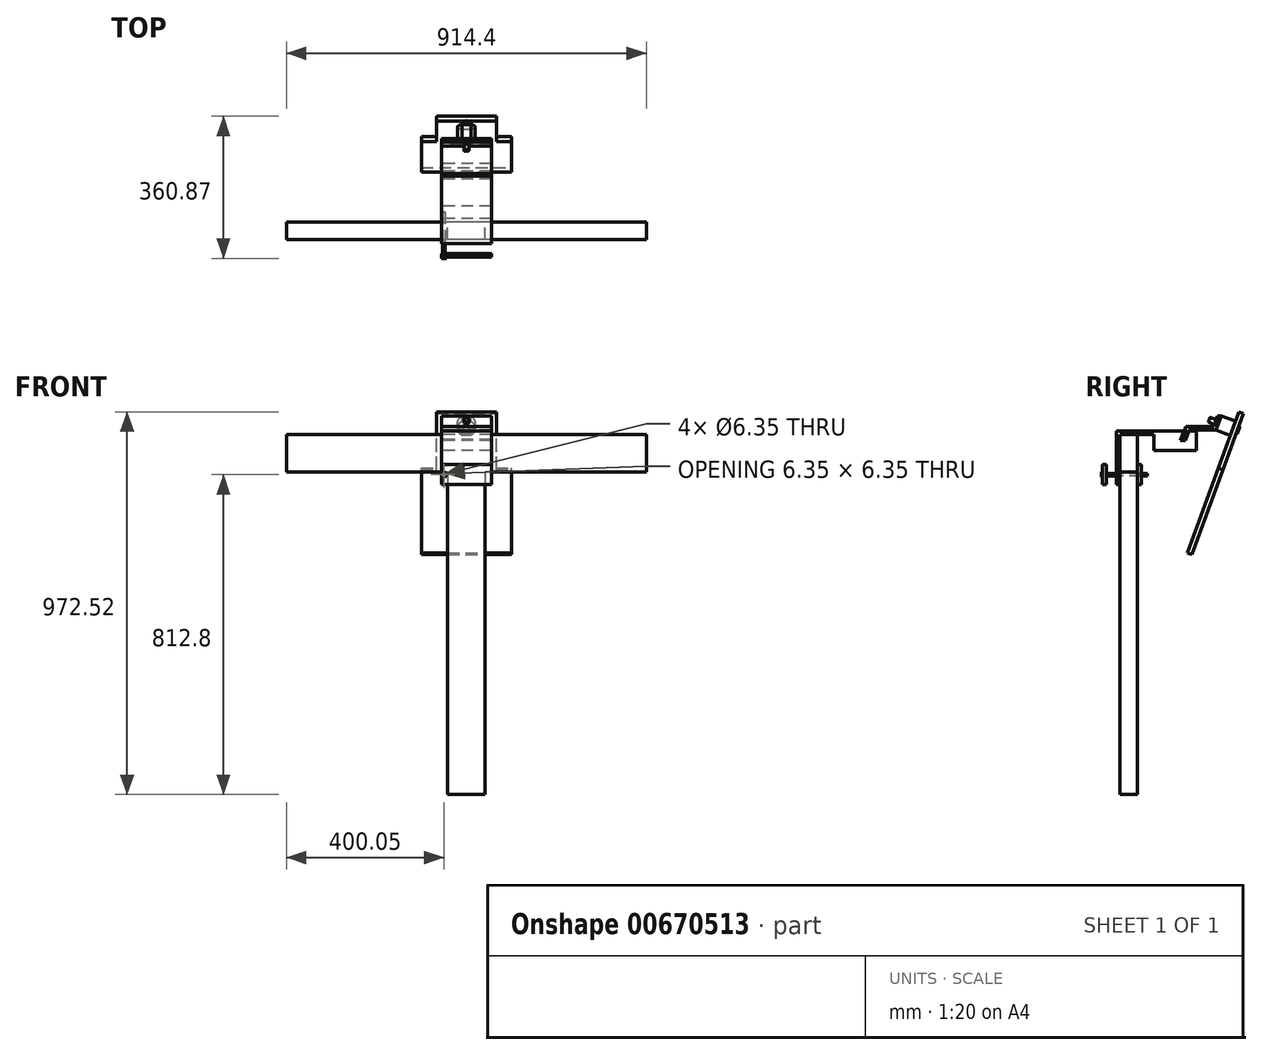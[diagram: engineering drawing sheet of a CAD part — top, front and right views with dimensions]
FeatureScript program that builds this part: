
annotation { "Feature Type Name" : "Feature", "Feature Type Description" : "" }
export const myFeature = defineFeature(function(context is Context, id is Id, definition is map)
    precondition{}
    {
        {
            var Q0;
            Q0=qCreatedBy(makeId("Right.planeOp"),FACE);
            var sketch = newSketch(context, id + "F0", { "sketchPlane" : qUnion([Q0])});
            skLineSegment(sketch, "E0.bottom", {"start": v(-44.45, 0) * mm, "end": v(0, 0) * mm});
            skLineSegment(sketch, "E0.top", {"start": v(-44.45, -914.4) * mm, "end": v(0, -914.4) * mm});
            skLineSegment(sketch, "E0.left", {"start": v(-44.45, 0) * mm, "end": v(-44.45, -914.4) * mm});
            skLineSegment(sketch, "E0.right", {"start": v(0, 0) * mm, "end": v(0, -914.4) * mm});
            skLineSegment(sketch, "E1.bottom", {"start": v(-53.97, 0) * mm, "end": v(149.23, 0) * mm});
            skLineSegment(sketch, "E1.top", {"start": v(-53.97, 9.52) * mm, "end": v(149.23, 9.53) * mm});
            skLineSegment(sketch, "E1.left", {"start": v(-53.98, 0) * mm, "end": v(-53.98, 9.53) * mm});
            skLineSegment(sketch, "E1.right", {"start": v(149.23, 0) * mm, "end": v(149.23, 9.53) * mm});
            skLineSegment(sketch, "E2.bottom", {"start": v(-53.97, 0) * mm, "end": v(-44.45, 0) * mm});
            skLineSegment(sketch, "E2.top", {"start": v(-53.97, -127) * mm, "end": v(-44.45, -127) * mm});
            skLineSegment(sketch, "E2.left", {"start": v(-53.97, 0) * mm, "end": v(-53.97, -127) * mm});
            skLineSegment(sketch, "E2.right", {"start": v(-44.45, 0) * mm, "end": v(-44.45, -127) * mm});
            skLineSegment(sketch, "E3.bottom", {"start": v(149.23, 0) * mm, "end": v(41.28, 0) * mm});
            skLineSegment(sketch, "E3.top", {"start": v(149.23, -39.75) * mm, "end": v(41.28, -39.75) * mm});
            skLineSegment(sketch, "E3.left", {"start": v(149.23, 0) * mm, "end": v(149.23, -39.75) * mm});
            skLineSegment(sketch, "E3.right", {"start": v(41.28, 0) * mm, "end": v(41.28, -39.75) * mm});
            skLineSegment(sketch, "E4", {"start": v(126.16, 33.39) * mm, "end": v(108.78, -14.35) * mm});
            skLineSegment(sketch, "E5", {"start": v(108.78, -14.35) * mm, "end": v(121.48, -14.35) * mm});
            skLineSegment(sketch, "E6", {"start": v(121.48, -14.35) * mm, "end": v(138.86, 33.39) * mm});
            skLineSegment(sketch, "E7.bottom", {"start": v(0, -127) * mm, "end": v(9.53, -127) * mm});
            skLineSegment(sketch, "E7.top", {"start": v(0, -76.2) * mm, "end": v(9.53, -76.2) * mm});
            skLineSegment(sketch, "E7.left", {"start": v(0, -127) * mm, "end": v(0, -76.2) * mm});
            skLineSegment(sketch, "E7.right", {"start": v(9.53, -127) * mm, "end": v(9.53, -76.2) * mm});
            skLineSegment(sketch, "E8", {"start": v(126.16, 33.39) * mm, "end": v(138.86, 33.39) * mm});
            skPoint(sketch, "E9", {"position": v(130.18, 9.52) * mm});
            skLineSegment(sketch, "E10", {"start": v(111.19, -11.81) * mm, "end": v(120.71, -11.81) * mm});
            skLineSegment(sketch, "E11", {"start": v(120.71, -11.81) * mm, "end": v(132.66, 21) * mm});
            skLineSegment(sketch, "E12", {"start": v(132.66, 21) * mm, "end": v(123.13, 21) * mm});
            skLineSegment(sketch, "E13", {"start": v(123.13, 21) * mm, "end": v(111.19, -11.81) * mm});
            skLineSegment(sketch, "E14.bottom", {"start": v(123.13, 21) * mm, "end": v(199.33, 21) * mm});
            skLineSegment(sketch, "E14.top", {"start": v(123.13, 11.48) * mm, "end": v(199.33, 11.48) * mm});
            skLineSegment(sketch, "E14.left", {"start": v(123.13, 21) * mm, "end": v(123.13, 11.48) * mm});
            skLineSegment(sketch, "E14.right", {"start": v(199.33, 21) * mm, "end": v(199.33, 11.48) * mm});
            skLineSegment(sketch, "E15", {"start": v(199.33, 11.48) * mm, "end": v(189.8, 11.48) * mm});
            skLineSegment(sketch, "E16", {"start": v(189.8, 11.48) * mm, "end": v(202.84, 47.29) * mm});
            skLineSegment(sketch, "E17", {"start": v(202.84, 47.29) * mm, "end": v(212.36, 47.29) * mm});
            skLineSegment(sketch, "E18", {"start": v(212.36, 47.29) * mm, "end": v(199.33, 11.48) * mm});
            skLineSegment(sketch, "E19.bottom", {"start": v(-88.9, -127) * mm, "end": v(-79.37, -127) * mm});
            skLineSegment(sketch, "E19.top", {"start": v(-88.9, -76.2) * mm, "end": v(-79.37, -76.2) * mm});
            skLineSegment(sketch, "E19.left", {"start": v(-88.9, -127) * mm, "end": v(-88.9, -76.2) * mm});
            skLineSegment(sketch, "E19.right", {"start": v(-79.37, -127) * mm, "end": v(-79.37, -76.2) * mm});
            skLineSegment(sketch, "E20.top", {"start": v(-44.45, -95.25) * mm, "end": v(0, -95.25) * mm});
            skLineSegment(sketch, "E20.left", {"start": v(-44.45, 0) * mm, "end": v(-44.45, -95.25) * mm});
            skLineSegment(sketch, "E20.right", {"start": v(0, 0) * mm, "end": v(0, -95.25) * mm});
            skSolve(sketch);
        }
        {
            var Q0;
            {var subQ1=sQuery(id+"F0.wireOp",EDGE,"E0.top");Q0=makeQuery(id+"F0.imprint","IMPRINT",FACE,{"disambiguationData":[TD([[makeQuery(id+"F0.imprint","IMPRINT",EDGE,{"derivedFrom":subQ1}),1.0]])]});}
            extrude(context, id + "F1", {"entities" : qUnion([Q0]), "depth" : 95.25 * mm, "offsetDistance" : 25.4 * mm, "symmetric" : true});
        }
        {
            var Q0;
            {var subQ2=sQuery(id+"F0.wireOp",EDGE,"E0.bottom");Q0=makeQuery(id+"F0.imprint","IMPRINT",FACE,{"disambiguationData":[TD([[makeQuery(id+"F0.imprint","IMPRINT",EDGE,{"derivedFrom":subQ2}),-1.0]])]});}
            extrude(context, id + "F2", {"entities" : qUnion([Q0]), "operationType" : NewBodyOperationType.ADD, "depth" : 914.4 * mm, "offsetDistance" : 25.4 * mm, "symmetric" : true});
        }
        {
            var Q0;
            {var subQ0=sQuery(id+"F0.wireOp",EDGE,"E2.top");Q0=makeQuery(id+"F0.imprint","IMPRINT",FACE,{"disambiguationData":[TD([[makeQuery(id+"F0.imprint","IMPRINT",EDGE,{"derivedFrom":subQ0}),1.0]])]});}
            var Q1;
            {var subQ1=sQuery(id+"F0.wireOp",EDGE,"E0.bottom");Q1=makeQuery(id+"F0.imprint","IMPRINT",FACE,{"disambiguationData":[TD([[makeQuery(id+"F0.imprint","IMPRINT",EDGE,{"derivedFrom":subQ1}),1.0]])]});}
            var Q2;
            Q2=makeQuery(id+"F0.imprint","IMPRINT",FACE,{"disambiguationData":[TD([[makeQuery(id+"F0.imprint","IMPRINT",EDGE,{"derivedFrom":sQuery(id+"F0.wireOp",EDGE,"E3.top")}),-1.0]])]});
            var Q3;
            {var subQ0=sQuery(id+"F0.wireOp",EDGE,"E1.right");Q3=makeQuery(id+"F0.imprint","IMPRINT",FACE,{"disambiguationData":[TD([[makeQuery(id+"F0.imprint","IMPRINT",EDGE,{"derivedFrom":subQ0}),1.0]])]});}
            var Q4;
            {var subQ3=sQuery(id+"F0.wireOp",EDGE,"E7.bottom");Q4=makeQuery(id+"F0.imprint","IMPRINT",FACE,{"disambiguationData":[TD([[makeQuery(id+"F0.imprint","IMPRINT",EDGE,{"derivedFrom":subQ3}),1.0]])]});}
            var Q5;
            Q5=makeQuery(id+"F0.imprint","IMPRINT",FACE,{"disambiguationData":[TD([[makeQuery(id+"F0.imprint","IMPRINT",EDGE,{"derivedFrom":sQuery(id+"F0.wireOp",EDGE,"E19.bottom")}),1.0]])]});
            extrude(context, id + "F3", {"entities" : qUnion([Q0, Q1, Q2, Q3, Q4, Q5]), "depth" : 127 * mm, "offsetDistance" : 25.4 * mm, "symmetric" : true});
        }
        {
            var Q0;
            {var subQ4=sQuery(id+"F0.wireOp",EDGE,"E14.right");Q0=makeQuery(id+"F0.imprint","IMPRINT",FACE,{"disambiguationData":[TD([[makeQuery(id+"F0.imprint","IMPRINT",EDGE,{"derivedFrom":subQ4}),1.0]])]});}
            var Q1;
            {var subQ0=sQuery(id+"F0.wireOp",EDGE,"E14.right");Q1=makeQuery(id+"F0.imprint","IMPRINT",FACE,{"disambiguationData":[TD([[makeQuery(id+"F0.imprint","IMPRINT",EDGE,{"derivedFrom":subQ0}),-1.0]])]});}
            var Q2;
            {var subQ0=sQuery(id+"F0.wireOp",EDGE,"E14.top");var subQ1=sQuery(id+"F0.wireOp",EDGE,"E6");var subQ2=makeQuery(id+"F0.imprint","INTERSECT",VERTEX,{"derivedFrom":[subQ1,subQ0]});Q2=makeQuery(id+"F0.imprint","IMPRINT",FACE,{"disambiguationData":[TD([[makeQuery(id+"F0.imprint","IMPRINT",EDGE,{"disambiguationData":[TD([[subQ2,-1.0]])],"derivedFrom":subQ1}),1.0]])]});}
            var Q3;
            {var subQ3=sQuery(id+"F0.wireOp",EDGE,"E12");Q3=makeQuery(id+"F0.imprint","IMPRINT",FACE,{"disambiguationData":[TD([[makeQuery(id+"F0.imprint","IMPRINT",EDGE,{"derivedFrom":subQ3}),1.0]])]});}
            var Q4;
            {var subQ3=sQuery(id+"F0.wireOp",EDGE,"E14.left");Q4=makeQuery(id+"F0.imprint","IMPRINT",FACE,{"disambiguationData":[TD([[makeQuery(id+"F0.imprint","IMPRINT",EDGE,{"derivedFrom":subQ3}),-1.0]])]});}
            var Q5;
            {var subQ0=sQuery(id+"F0.wireOp",EDGE,"E13");var subQ1=sQuery(id+"F0.wireOp",EDGE,"E1.bottom");var subQ2=makeQuery(id+"F0.imprint","INTERSECT",VERTEX,{"derivedFrom":[subQ1,subQ0]});Q5=makeQuery(id+"F0.imprint","IMPRINT",FACE,{"disambiguationData":[TD([[makeQuery(id+"F0.imprint","IMPRINT",EDGE,{"disambiguationData":[TD([[subQ2,-1.0]])],"derivedFrom":subQ1}),1.0]])]});}
            var Q6;
            {var subQ5=sQuery(id+"F0.wireOp",EDGE,"E10");Q6=makeQuery(id+"F0.imprint","IMPRINT",FACE,{"disambiguationData":[TD([[makeQuery(id+"F0.imprint","IMPRINT",EDGE,{"derivedFrom":subQ5}),1.0]])]});}
            var Q7;
            {var subQ0=sQuery(id+"F0.wireOp",EDGE,"E14.top");var subQ1=sQuery(id+"F0.wireOp",EDGE,"E6");var subQ2=makeQuery(id+"F0.imprint","INTERSECT",VERTEX,{"derivedFrom":[subQ1,subQ0]});Q7=makeQuery(id+"F0.imprint","IMPRINT",FACE,{"disambiguationData":[TD([[makeQuery(id+"F0.imprint","IMPRINT",EDGE,{"disambiguationData":[TD([[subQ2,-1.0]])],"derivedFrom":subQ1}),-1.0]])]});}
            extrude(context, id + "F4", {"entities" : qUnion([Q0, Q1, Q2, Q3, Q4, Q5, Q6, Q7]), "depth" : 127 * mm, "offsetDistance" : 25.4 * mm, "symmetric" : true});
        }
        {
            var Q0;
            Q0=makeQuery(id+"F4.opExtrude","SWEPT_FACE",FACE,{"disambiguationData":[OSD([sQuery(id+"F0.wireOp",EDGE,"E18")])]});
            var sketch = newSketch(context, id + "F5", { "sketchPlane" : qUnion([Q0])});
            skCircle(sketch, "E21", {"center": v(0, 98.02) * mm, "radius": 6.35 * mm});
            skCircle(sketch, "E22", {"center": v(0, 98.02) * mm, "radius": 22.23 * mm});
            skSolve(sketch);
        }
        {
            var Q0;
            {var subQ0=sQuery(id+"F5.wireOp",EDGE,"E22");var subQ1=makeQuery(id+"F4.opExtrude","SWEPT_EDGE",EDGE,{"disambiguationData":[OSD([sQuery(id+"F0.wireOp",EDGE,"E17"),sQuery(id+"F0.wireOp",EDGE,"E18")])]});var subQ2=makeQuery(id+"F5.imprint","INTERSECT",VERTEX,{"disambiguationData":[OD(0.0)],"derivedFrom":[subQ1,subQ0]});Q0=makeQuery(id+"F5.imprint","IMPRINT",FACE,{"disambiguationData":[TD([[makeQuery(id+"F5.imprint","IMPRINT",EDGE,{"disambiguationData":[TD([[subQ2,1.0]])],"derivedFrom":subQ0}),1.0]])]});}
            var Q1;
            Q1=makeQuery(id+"F5.imprint","IMPRINT",FACE,{"disambiguationData":[TD([[makeQuery(id+"F5.imprint","IMPRINT",EDGE,{"derivedFrom":sQuery(id+"F5.wireOp",EDGE,"E21")}),-1.0]])]});
            var Q2;
            {var subQ0=sQuery(id+"F5.wireOp",EDGE,"E22");var subQ1=makeQuery(id+"F4.opExtrude","SWEPT_EDGE",EDGE,{"disambiguationData":[OSD([sQuery(id+"F0.wireOp",EDGE,"E14.top"),sQuery(id+"F0.wireOp",EDGE,"E14.right"),sQuery(id+"F0.wireOp",EDGE,"E18")])]});var subQ2=makeQuery(id+"F5.imprint","INTERSECT",VERTEX,{"disambiguationData":[OD(0.0)],"derivedFrom":[subQ1,subQ0]});Q2=makeQuery(id+"F5.imprint","IMPRINT",FACE,{"disambiguationData":[TD([[makeQuery(id+"F5.imprint","IMPRINT",EDGE,{"disambiguationData":[TD([[subQ2,-1.0]])],"derivedFrom":subQ0}),1.0]])]});}
            extrude(context, id + "F6", {"entities" : qUnion([Q0, Q1, Q2]), "depth" : 38.1 * mm, "offsetDistance" : 25.4 * mm});
        }
        {
            var Q0;
            Q0=makeQuery(id+"F6.opExtrude","CAP_FACE",FACE,{"disambiguationData":[OSD([sQuery(id+"F5.wireOp",EDGE,"E21"),sQuery(id+"F5.wireOp",EDGE,"E22")])],"isStart":false});
            var sketch = newSketch(context, id + "F7", { "sketchPlane" : qUnion([Q0])});
            skLineSegment(sketch, "E23.bottom", {"start": v(76.2, -9.93) * mm, "end": v(-76.2, -9.93) * mm});
            skLineSegment(sketch, "E23.top", {"start": v(76.2, 142.47) * mm, "end": v(-76.2, 142.47) * mm});
            skLineSegment(sketch, "E23.left", {"start": v(76.2, -9.93) * mm, "end": v(76.2, 142.47) * mm});
            skLineSegment(sketch, "E23.right", {"start": v(-76.2, -9.93) * mm, "end": v(-76.2, 142.47) * mm});
            skPoint(sketch, "E23.middle", {"position": v(0, 66.27) * mm});
            skLineSegment(sketch, "E24.bottom", {"start": v(114.3, -238.53) * mm, "end": v(-114.3, -238.53) * mm});
            skLineSegment(sketch, "E24.top", {"start": v(114.3, -9.93) * mm, "end": v(-114.3, -9.93) * mm});
            skLineSegment(sketch, "E24.left", {"start": v(114.3, -238.53) * mm, "end": v(114.3, -9.93) * mm});
            skLineSegment(sketch, "E24.right", {"start": v(-114.3, -238.53) * mm, "end": v(-114.3, -9.93) * mm});
            skPoint(sketch, "E24.middle", {"position": v(0, -124.23) * mm});
            skSolve(sketch);
        }
        {
            var Q0;
            Q0 = qSketchRegion(id + "F7", true);
            extrude(context, id + "F8", {"entities" : qUnion([Q0]), "depth" : 12.7 * mm, "offsetDistance" : 25.4 * mm});
        }
        {
            var Q0;
            Q0=makeQuery(id+"F5.imprint","IMPRINT",FACE,{"disambiguationData":[TD([[makeQuery(id+"F5.imprint","IMPRINT",EDGE,{"derivedFrom":sQuery(id+"F5.wireOp",EDGE,"E21")}),1.0]])]});
            extrude(context, id + "F9", {"entities" : qUnion([Q0]), "operationType" : NewBodyOperationType.REMOVE, "depth" : 152.4 * mm, "offsetDistance" : 25.4 * mm, "symmetric" : true});
        }
        {
            var Q0;
            Q0=makeQuery(id+"F8.opExtrude","CAP_FACE",FACE,{"disambiguationData":[OSD([sQuery(id+"F7.wireOp",EDGE,"E23.top"),sQuery(id+"F7.wireOp",EDGE,"E23.left"),sQuery(id+"F7.wireOp",EDGE,"E23.right"),sQuery(id+"F7.wireOp",EDGE,"E24.bottom"),sQuery(id+"F7.wireOp",EDGE,"E24.top"),sQuery(id+"F7.wireOp",EDGE,"E24.left"),sQuery(id+"F7.wireOp",EDGE,"E24.right")])],"isStart":false});
            var sketch = newSketch(context, id + "F10", { "sketchPlane" : qUnion([Q0])});
            skCircle(sketch, "E25", {"center": v(0, 98.02) * mm, "radius": 9.53 * mm});
            skCircle(sketch, "E26", {"center": v(0, 98.02) * mm, "radius": 6.35 * mm});
            skSolve(sketch);
        }
        {
            var Q0;
            Q0=makeQuery(id+"F10.imprint","IMPRINT",FACE,{"disambiguationData":[TD([[makeQuery(id+"F10.imprint","IMPRINT",EDGE,{"derivedFrom":sQuery(id+"F10.wireOp",EDGE,"E25")}),1.0]])]});
            var Q1;
            Q1=makeQuery(id+"F10.imprint","IMPRINT",FACE,{"disambiguationData":[TD([[makeQuery(id+"F10.imprint","IMPRINT",EDGE,{"derivedFrom":sQuery(id+"F10.wireOp",EDGE,"E26")}),-1.0]])]});
            extrude(context, id + "F11", {"entities" : qUnion([Q0, Q1]), "depth" : 3.17 * mm, "offsetDistance" : 25.4 * mm});
        }
        {
            var Q0;
            Q0=makeQuery(id+"F10.imprint","IMPRINT",FACE,{"disambiguationData":[TD([[makeQuery(id+"F10.imprint","IMPRINT",EDGE,{"derivedFrom":sQuery(id+"F10.wireOp",EDGE,"E26")}),-1.0]])]});
            extrude(context, id + "F12", {"entities" : qUnion([Q0]), "operationType" : NewBodyOperationType.ADD, "oppositeDirection" : true, "depth" : 76.2 * mm, "offsetDistance" : 25.4 * mm});
        }
        {
            var Q0;
            Q0=makeQuery(id+"F3.opExtrude","SWEPT_FACE",FACE,{"disambiguationData":[OSD([sQuery(id+"F0.wireOp",EDGE,"E19.left")])]});
            var sketch = newSketch(context, id + "F13", { "sketchPlane" : qUnion([Q0])});
            skCircle(sketch, "E27", {"center": v(-57.15, -101.6) * mm, "radius": 3.18 * mm});
            skPoint(sketch, "E28", {"position": v(-63.5, -101.6) * mm});
            skCircle(sketch, "E29", {"center": v(-57.15, -101.6) * mm, "radius": 6.35 * mm});
            skSolve(sketch);
        }
        {
            var Q0;
            Q0=makeQuery(id+"F13.imprint","IMPRINT",FACE,{"disambiguationData":[TD([[makeQuery(id+"F13.imprint","IMPRINT",EDGE,{"derivedFrom":sQuery(id+"F13.wireOp",EDGE,"E27")}),1.0]])]});
            extrude(context, id + "F14", {"entities" : qUnion([Q0]), "operationType" : NewBodyOperationType.REMOVE, "oppositeDirection" : true, "depth" : 127 * mm, "offsetDistance" : 25.4 * mm});
        }
        {
            var Q0;
            Q0=makeQuery(id+"F13.imprint","IMPRINT",FACE,{"disambiguationData":[TD([[makeQuery(id+"F13.imprint","IMPRINT",EDGE,{"derivedFrom":sQuery(id+"F13.wireOp",EDGE,"E27")}),1.0]])]});
            extrude(context, id + "F15", {"entities" : qUnion([Q0]), "oppositeDirection" : true, "depth" : 114.3 * mm, "offsetDistance" : 25.4 * mm});
        }
        {
            var Q0;
            Q0=makeQuery(id+"F13.imprint","IMPRINT",FACE,{"disambiguationData":[TD([[makeQuery(id+"F13.imprint","IMPRINT",EDGE,{"derivedFrom":sQuery(id+"F13.wireOp",EDGE,"E27")}),-1.0]])]});
            var Q1;
            Q1=makeQuery(id+"F13.imprint","IMPRINT",FACE,{"disambiguationData":[TD([[makeQuery(id+"F13.imprint","IMPRINT",EDGE,{"derivedFrom":sQuery(id+"F13.wireOp",EDGE,"E27")}),1.0]])]});
            extrude(context, id + "F16", {"entities" : qUnion([Q0, Q1]), "operationType" : NewBodyOperationType.ADD, "depth" : 3.17 * mm, "offsetDistance" : 25.4 * mm});
        }
    });
